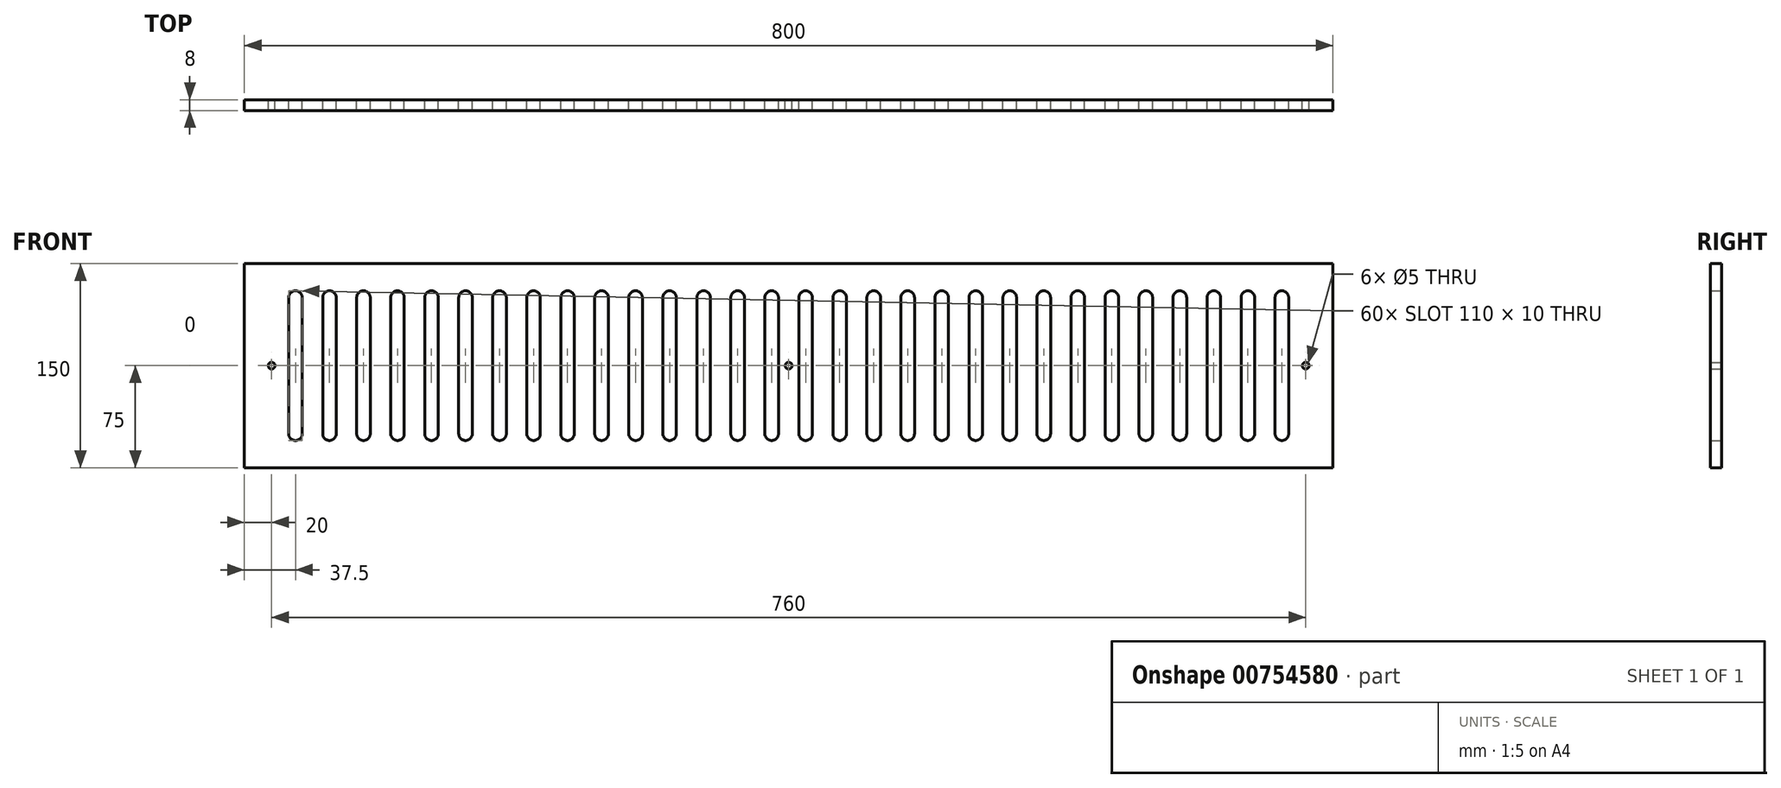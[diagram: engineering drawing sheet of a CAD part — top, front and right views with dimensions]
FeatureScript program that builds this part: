
annotation { "Feature Type Name" : "Feature", "Feature Type Description" : "" }
export const myFeature = defineFeature(function(context is Context, id is Id, definition is map)
    precondition{}
    {
        {
            var Q0;
            Q0=qCreatedBy(makeId("Front.planeOp"),FACE);
            var sketch = newSketch(context, id + "F0", { "sketchPlane" : qUnion([Q0])});
            skCircle(sketch, "E0", {"center": v(0, 0) * mm, "radius": 2.5 * mm});
            skLineSegment(sketch, "E1.bottom", {"start": v(400, 75) * mm, "end": v(-400, 75) * mm});
            skLineSegment(sketch, "E1.top", {"start": v(400, -75) * mm, "end": v(-400, -75) * mm});
            skLineSegment(sketch, "E1.left", {"start": v(400, 75) * mm, "end": v(400, -75) * mm});
            skLineSegment(sketch, "E1.right", {"start": v(-400, 75) * mm, "end": v(-400, -75) * mm});
            skLineSegment(sketch, "E2", {"start": v(-400, 0) * mm, "end": v(400, 0) * mm});
            skCircle(sketch, "E3", {"center": v(-380, 0) * mm, "radius": 2.5 * mm});
            skLineSegment(sketch, "E4.bottom", {"start": v(-362.5, 55) * mm, "end": v(-362.5, 55) * mm});
            skLineSegment(sketch, "E4.top", {"start": v(-362.5, -55) * mm, "end": v(-362.5, -55) * mm});
            skLineSegment(sketch, "E4.left", {"start": v(-357.5, 50) * mm, "end": v(-357.5, -50) * mm});
            skLineSegment(sketch, "E4.right", {"start": v(-367.5, 50) * mm, "end": v(-367.5, -50) * mm});
            skPoint(sketch, "E4.middle", {"position": v(-362.5, 0) * mm});
            skPoint(sketch, "E5.visualSharp", {"position": v(-367.5, 55) * mm});
            skArc(sketch, "E5.filletArc", {"start": v(-362.5, 55) * mm, "mid": v(-366.04, 53.54) * mm, "end": v(-367.5, 50) * mm});
            skPoint(sketch, "E6.visualSharp", {"position": v(-357.5, 55) * mm});
            skArc(sketch, "E6.filletArc", {"start": v(-357.5, 50) * mm, "mid": v(-358.96, 53.54) * mm, "end": v(-362.5, 55) * mm});
            skPoint(sketch, "E7.visualSharp", {"position": v(-357.5, -55) * mm});
            skArc(sketch, "E7.filletArc", {"start": v(-362.5, -55) * mm, "mid": v(-358.96, -53.54) * mm, "end": v(-357.5, -50) * mm});
            skPoint(sketch, "E8.visualSharp", {"position": v(-367.5, -55) * mm});
            skArc(sketch, "E8.filletArc", {"start": v(-367.5, -50) * mm, "mid": v(-366.04, -53.54) * mm, "end": v(-362.5, -55) * mm});
            skLineSegment(sketch, "E9.1.0.0", {"start": v(-332.5, 50) * mm, "end": v(-332.5, -50) * mm});
            skLineSegment(sketch, "E9.1.0.1", {"start": v(-342.5, 50) * mm, "end": v(-342.5, -50) * mm});
            skPoint(sketch, "E9.1.0.2", {"position": v(-342.5, -55) * mm});
            skPoint(sketch, "E9.1.0.3", {"position": v(-342.5, 55) * mm});
            skPoint(sketch, "E9.1.0.4", {"position": v(-332.5, 55) * mm});
            skPoint(sketch, "E9.1.0.5", {"position": v(-337.5, 0) * mm});
            skPoint(sketch, "E9.1.0.6", {"position": v(-332.5, -55) * mm});
            skArc(sketch, "E9.1.0.7", {"start": v(-332.5, 50) * mm, "mid": v(-333.96, 53.54) * mm, "end": v(-337.5, 55) * mm});
            skArc(sketch, "E9.1.0.8", {"start": v(-342.5, -50) * mm, "mid": v(-341.04, -53.54) * mm, "end": v(-337.5, -55) * mm});
            skArc(sketch, "E9.1.0.9", {"start": v(-337.5, -55) * mm, "mid": v(-333.96, -53.54) * mm, "end": v(-332.5, -50) * mm});
            skArc(sketch, "E9.1.0.10", {"start": v(-337.5, 55) * mm, "mid": v(-341.04, 53.54) * mm, "end": v(-342.5, 50) * mm});
            skLineSegment(sketch, "E9.2.0.0", {"start": v(-307.5, 50) * mm, "end": v(-307.5, -50) * mm});
            skLineSegment(sketch, "E9.2.0.1", {"start": v(-317.5, 50) * mm, "end": v(-317.5, -50) * mm});
            skPoint(sketch, "E9.2.0.2", {"position": v(-317.5, -55) * mm});
            skPoint(sketch, "E9.2.0.3", {"position": v(-317.5, 55) * mm});
            skPoint(sketch, "E9.2.0.4", {"position": v(-307.5, 55) * mm});
            skPoint(sketch, "E9.2.0.5", {"position": v(-312.5, 0) * mm});
            skPoint(sketch, "E9.2.0.6", {"position": v(-307.5, -55) * mm});
            skArc(sketch, "E9.2.0.7", {"start": v(-307.5, 50) * mm, "mid": v(-308.96, 53.54) * mm, "end": v(-312.5, 55) * mm});
            skArc(sketch, "E9.2.0.8", {"start": v(-317.5, -50) * mm, "mid": v(-316.04, -53.54) * mm, "end": v(-312.5, -55) * mm});
            skArc(sketch, "E9.2.0.9", {"start": v(-312.5, -55) * mm, "mid": v(-308.96, -53.54) * mm, "end": v(-307.5, -50) * mm});
            skArc(sketch, "E9.2.0.10", {"start": v(-312.5, 55) * mm, "mid": v(-316.04, 53.54) * mm, "end": v(-317.5, 50) * mm});
            skLineSegment(sketch, "E9.3.0.0", {"start": v(-282.5, 50) * mm, "end": v(-282.5, -50) * mm});
            skLineSegment(sketch, "E9.3.0.1", {"start": v(-292.5, 50) * mm, "end": v(-292.5, -50) * mm});
            skPoint(sketch, "E9.3.0.2", {"position": v(-292.5, -55) * mm});
            skPoint(sketch, "E9.3.0.3", {"position": v(-292.5, 55) * mm});
            skPoint(sketch, "E9.3.0.4", {"position": v(-282.5, 55) * mm});
            skPoint(sketch, "E9.3.0.5", {"position": v(-287.5, 0) * mm});
            skPoint(sketch, "E9.3.0.6", {"position": v(-282.5, -55) * mm});
            skArc(sketch, "E9.3.0.7", {"start": v(-282.5, 50) * mm, "mid": v(-283.96, 53.54) * mm, "end": v(-287.5, 55) * mm});
            skArc(sketch, "E9.3.0.8", {"start": v(-292.5, -50) * mm, "mid": v(-291.04, -53.54) * mm, "end": v(-287.5, -55) * mm});
            skArc(sketch, "E9.3.0.9", {"start": v(-287.5, -55) * mm, "mid": v(-283.96, -53.54) * mm, "end": v(-282.5, -50) * mm});
            skArc(sketch, "E9.3.0.10", {"start": v(-287.5, 55) * mm, "mid": v(-291.04, 53.54) * mm, "end": v(-292.5, 50) * mm});
            skLineSegment(sketch, "E9.4.0.0", {"start": v(-257.5, 50) * mm, "end": v(-257.5, -50) * mm});
            skLineSegment(sketch, "E9.4.0.1", {"start": v(-267.5, 50) * mm, "end": v(-267.5, -50) * mm});
            skPoint(sketch, "E9.4.0.2", {"position": v(-267.5, -55) * mm});
            skPoint(sketch, "E9.4.0.3", {"position": v(-267.5, 55) * mm});
            skPoint(sketch, "E9.4.0.4", {"position": v(-257.5, 55) * mm});
            skPoint(sketch, "E9.4.0.5", {"position": v(-262.5, 0) * mm});
            skPoint(sketch, "E9.4.0.6", {"position": v(-257.5, -55) * mm});
            skArc(sketch, "E9.4.0.7", {"start": v(-257.5, 50) * mm, "mid": v(-258.96, 53.54) * mm, "end": v(-262.5, 55) * mm});
            skArc(sketch, "E9.4.0.8", {"start": v(-267.5, -50) * mm, "mid": v(-266.04, -53.54) * mm, "end": v(-262.5, -55) * mm});
            skArc(sketch, "E9.4.0.9", {"start": v(-262.5, -55) * mm, "mid": v(-258.96, -53.54) * mm, "end": v(-257.5, -50) * mm});
            skArc(sketch, "E9.4.0.10", {"start": v(-262.5, 55) * mm, "mid": v(-266.04, 53.54) * mm, "end": v(-267.5, 50) * mm});
            skLineSegment(sketch, "E9.5.0.0", {"start": v(-232.5, 50) * mm, "end": v(-232.5, -50) * mm});
            skLineSegment(sketch, "E9.5.0.1", {"start": v(-242.5, 50) * mm, "end": v(-242.5, -50) * mm});
            skPoint(sketch, "E9.5.0.2", {"position": v(-242.5, -55) * mm});
            skPoint(sketch, "E9.5.0.3", {"position": v(-242.5, 55) * mm});
            skPoint(sketch, "E9.5.0.4", {"position": v(-232.5, 55) * mm});
            skPoint(sketch, "E9.5.0.5", {"position": v(-237.5, 0) * mm});
            skPoint(sketch, "E9.5.0.6", {"position": v(-232.5, -55) * mm});
            skArc(sketch, "E9.5.0.7", {"start": v(-232.5, 50) * mm, "mid": v(-233.96, 53.54) * mm, "end": v(-237.5, 55) * mm});
            skArc(sketch, "E9.5.0.8", {"start": v(-242.5, -50) * mm, "mid": v(-241.04, -53.54) * mm, "end": v(-237.5, -55) * mm});
            skArc(sketch, "E9.5.0.9", {"start": v(-237.5, -55) * mm, "mid": v(-233.96, -53.54) * mm, "end": v(-232.5, -50) * mm});
            skArc(sketch, "E9.5.0.10", {"start": v(-237.5, 55) * mm, "mid": v(-241.04, 53.54) * mm, "end": v(-242.5, 50) * mm});
            skLineSegment(sketch, "E9.6.0.0", {"start": v(-207.5, 50) * mm, "end": v(-207.5, -50) * mm});
            skLineSegment(sketch, "E9.6.0.1", {"start": v(-217.5, 50) * mm, "end": v(-217.5, -50) * mm});
            skPoint(sketch, "E9.6.0.2", {"position": v(-217.5, -55) * mm});
            skPoint(sketch, "E9.6.0.3", {"position": v(-217.5, 55) * mm});
            skPoint(sketch, "E9.6.0.4", {"position": v(-207.5, 55) * mm});
            skPoint(sketch, "E9.6.0.5", {"position": v(-212.5, 0) * mm});
            skPoint(sketch, "E9.6.0.6", {"position": v(-207.5, -55) * mm});
            skArc(sketch, "E9.6.0.7", {"start": v(-207.5, 50) * mm, "mid": v(-208.96, 53.54) * mm, "end": v(-212.5, 55) * mm});
            skArc(sketch, "E9.6.0.8", {"start": v(-217.5, -50) * mm, "mid": v(-216.04, -53.54) * mm, "end": v(-212.5, -55) * mm});
            skArc(sketch, "E9.6.0.9", {"start": v(-212.5, -55) * mm, "mid": v(-208.96, -53.54) * mm, "end": v(-207.5, -50) * mm});
            skArc(sketch, "E9.6.0.10", {"start": v(-212.5, 55) * mm, "mid": v(-216.04, 53.54) * mm, "end": v(-217.5, 50) * mm});
            skLineSegment(sketch, "E9.7.0.0", {"start": v(-182.5, 50) * mm, "end": v(-182.5, -50) * mm});
            skLineSegment(sketch, "E9.7.0.1", {"start": v(-192.5, 50) * mm, "end": v(-192.5, -50) * mm});
            skPoint(sketch, "E9.7.0.2", {"position": v(-192.5, -55) * mm});
            skPoint(sketch, "E9.7.0.3", {"position": v(-192.5, 55) * mm});
            skPoint(sketch, "E9.7.0.4", {"position": v(-182.5, 55) * mm});
            skPoint(sketch, "E9.7.0.5", {"position": v(-187.5, 0) * mm});
            skPoint(sketch, "E9.7.0.6", {"position": v(-182.5, -55) * mm});
            skArc(sketch, "E9.7.0.7", {"start": v(-182.5, 50) * mm, "mid": v(-183.96, 53.54) * mm, "end": v(-187.5, 55) * mm});
            skArc(sketch, "E9.7.0.8", {"start": v(-192.5, -50) * mm, "mid": v(-191.04, -53.54) * mm, "end": v(-187.5, -55) * mm});
            skArc(sketch, "E9.7.0.9", {"start": v(-187.5, -55) * mm, "mid": v(-183.96, -53.54) * mm, "end": v(-182.5, -50) * mm});
            skArc(sketch, "E9.7.0.10", {"start": v(-187.5, 55) * mm, "mid": v(-191.04, 53.54) * mm, "end": v(-192.5, 50) * mm});
            skLineSegment(sketch, "E9.8.0.0", {"start": v(-157.5, 50) * mm, "end": v(-157.5, -50) * mm});
            skLineSegment(sketch, "E9.8.0.1", {"start": v(-167.5, 50) * mm, "end": v(-167.5, -50) * mm});
            skPoint(sketch, "E9.8.0.2", {"position": v(-167.5, -55) * mm});
            skPoint(sketch, "E9.8.0.3", {"position": v(-167.5, 55) * mm});
            skPoint(sketch, "E9.8.0.4", {"position": v(-157.5, 55) * mm});
            skPoint(sketch, "E9.8.0.5", {"position": v(-162.5, 0) * mm});
            skPoint(sketch, "E9.8.0.6", {"position": v(-157.5, -55) * mm});
            skArc(sketch, "E9.8.0.7", {"start": v(-157.5, 50) * mm, "mid": v(-158.96, 53.54) * mm, "end": v(-162.5, 55) * mm});
            skArc(sketch, "E9.8.0.8", {"start": v(-167.5, -50) * mm, "mid": v(-166.04, -53.54) * mm, "end": v(-162.5, -55) * mm});
            skArc(sketch, "E9.8.0.9", {"start": v(-162.5, -55) * mm, "mid": v(-158.96, -53.54) * mm, "end": v(-157.5, -50) * mm});
            skArc(sketch, "E9.8.0.10", {"start": v(-162.5, 55) * mm, "mid": v(-166.04, 53.54) * mm, "end": v(-167.5, 50) * mm});
            skLineSegment(sketch, "E9.9.0.0", {"start": v(-132.5, 50) * mm, "end": v(-132.5, -50) * mm});
            skLineSegment(sketch, "E9.9.0.1", {"start": v(-142.5, 50) * mm, "end": v(-142.5, -50) * mm});
            skPoint(sketch, "E9.9.0.2", {"position": v(-142.5, -55) * mm});
            skPoint(sketch, "E9.9.0.3", {"position": v(-142.5, 55) * mm});
            skPoint(sketch, "E9.9.0.4", {"position": v(-132.5, 55) * mm});
            skPoint(sketch, "E9.9.0.5", {"position": v(-137.5, 0) * mm});
            skPoint(sketch, "E9.9.0.6", {"position": v(-132.5, -55) * mm});
            skArc(sketch, "E9.9.0.7", {"start": v(-132.5, 50) * mm, "mid": v(-133.96, 53.54) * mm, "end": v(-137.5, 55) * mm});
            skArc(sketch, "E9.9.0.8", {"start": v(-142.5, -50) * mm, "mid": v(-141.04, -53.54) * mm, "end": v(-137.5, -55) * mm});
            skArc(sketch, "E9.9.0.9", {"start": v(-137.5, -55) * mm, "mid": v(-133.96, -53.54) * mm, "end": v(-132.5, -50) * mm});
            skArc(sketch, "E9.9.0.10", {"start": v(-137.5, 55) * mm, "mid": v(-141.04, 53.54) * mm, "end": v(-142.5, 50) * mm});
            skLineSegment(sketch, "E9.10.0.0", {"start": v(-107.5, 50) * mm, "end": v(-107.5, -50) * mm});
            skLineSegment(sketch, "E9.10.0.1", {"start": v(-117.5, 50) * mm, "end": v(-117.5, -50) * mm});
            skPoint(sketch, "E9.10.0.2", {"position": v(-117.5, -55) * mm});
            skPoint(sketch, "E9.10.0.3", {"position": v(-117.5, 55) * mm});
            skPoint(sketch, "E9.10.0.4", {"position": v(-107.5, 55) * mm});
            skPoint(sketch, "E9.10.0.5", {"position": v(-112.5, 0) * mm});
            skPoint(sketch, "E9.10.0.6", {"position": v(-107.5, -55) * mm});
            skArc(sketch, "E9.10.0.7", {"start": v(-107.5, 50) * mm, "mid": v(-108.96, 53.54) * mm, "end": v(-112.5, 55) * mm});
            skArc(sketch, "E9.10.0.8", {"start": v(-117.5, -50) * mm, "mid": v(-116.04, -53.54) * mm, "end": v(-112.5, -55) * mm});
            skArc(sketch, "E9.10.0.9", {"start": v(-112.5, -55) * mm, "mid": v(-108.96, -53.54) * mm, "end": v(-107.5, -50) * mm});
            skArc(sketch, "E9.10.0.10", {"start": v(-112.5, 55) * mm, "mid": v(-116.04, 53.54) * mm, "end": v(-117.5, 50) * mm});
            skLineSegment(sketch, "E9.11.0.0", {"start": v(-82.5, 50) * mm, "end": v(-82.5, -50) * mm});
            skLineSegment(sketch, "E9.11.0.1", {"start": v(-92.5, 50) * mm, "end": v(-92.5, -50) * mm});
            skPoint(sketch, "E9.11.0.2", {"position": v(-92.5, -55) * mm});
            skPoint(sketch, "E9.11.0.3", {"position": v(-92.5, 55) * mm});
            skPoint(sketch, "E9.11.0.4", {"position": v(-82.5, 55) * mm});
            skPoint(sketch, "E9.11.0.5", {"position": v(-87.5, 0) * mm});
            skPoint(sketch, "E9.11.0.6", {"position": v(-82.5, -55) * mm});
            skArc(sketch, "E9.11.0.7", {"start": v(-82.5, 50) * mm, "mid": v(-83.96, 53.54) * mm, "end": v(-87.5, 55) * mm});
            skArc(sketch, "E9.11.0.8", {"start": v(-92.5, -50) * mm, "mid": v(-91.04, -53.54) * mm, "end": v(-87.5, -55) * mm});
            skArc(sketch, "E9.11.0.9", {"start": v(-87.5, -55) * mm, "mid": v(-83.96, -53.54) * mm, "end": v(-82.5, -50) * mm});
            skArc(sketch, "E9.11.0.10", {"start": v(-87.5, 55) * mm, "mid": v(-91.04, 53.54) * mm, "end": v(-92.5, 50) * mm});
            skLineSegment(sketch, "E9.12.0.0", {"start": v(-57.5, 50) * mm, "end": v(-57.5, -50) * mm});
            skLineSegment(sketch, "E9.12.0.1", {"start": v(-67.5, 50) * mm, "end": v(-67.5, -50) * mm});
            skPoint(sketch, "E9.12.0.2", {"position": v(-67.5, -55) * mm});
            skPoint(sketch, "E9.12.0.3", {"position": v(-67.5, 55) * mm});
            skPoint(sketch, "E9.12.0.4", {"position": v(-57.5, 55) * mm});
            skPoint(sketch, "E9.12.0.5", {"position": v(-62.5, 0) * mm});
            skPoint(sketch, "E9.12.0.6", {"position": v(-57.5, -55) * mm});
            skArc(sketch, "E9.12.0.7", {"start": v(-57.5, 50) * mm, "mid": v(-58.96, 53.54) * mm, "end": v(-62.5, 55) * mm});
            skArc(sketch, "E9.12.0.8", {"start": v(-67.5, -50) * mm, "mid": v(-66.04, -53.54) * mm, "end": v(-62.5, -55) * mm});
            skArc(sketch, "E9.12.0.9", {"start": v(-62.5, -55) * mm, "mid": v(-58.96, -53.54) * mm, "end": v(-57.5, -50) * mm});
            skArc(sketch, "E9.12.0.10", {"start": v(-62.5, 55) * mm, "mid": v(-66.04, 53.54) * mm, "end": v(-67.5, 50) * mm});
            skLineSegment(sketch, "E9.13.0.0", {"start": v(-32.5, 50) * mm, "end": v(-32.5, -50) * mm});
            skLineSegment(sketch, "E9.13.0.1", {"start": v(-42.5, 50) * mm, "end": v(-42.5, -50) * mm});
            skPoint(sketch, "E9.13.0.2", {"position": v(-42.5, -55) * mm});
            skPoint(sketch, "E9.13.0.3", {"position": v(-42.5, 55) * mm});
            skPoint(sketch, "E9.13.0.4", {"position": v(-32.5, 55) * mm});
            skPoint(sketch, "E9.13.0.5", {"position": v(-37.5, 0) * mm});
            skPoint(sketch, "E9.13.0.6", {"position": v(-32.5, -55) * mm});
            skArc(sketch, "E9.13.0.7", {"start": v(-32.5, 50) * mm, "mid": v(-33.96, 53.54) * mm, "end": v(-37.5, 55) * mm});
            skArc(sketch, "E9.13.0.8", {"start": v(-42.5, -50) * mm, "mid": v(-41.04, -53.54) * mm, "end": v(-37.5, -55) * mm});
            skArc(sketch, "E9.13.0.9", {"start": v(-37.5, -55) * mm, "mid": v(-33.96, -53.54) * mm, "end": v(-32.5, -50) * mm});
            skArc(sketch, "E9.13.0.10", {"start": v(-37.5, 55) * mm, "mid": v(-41.04, 53.54) * mm, "end": v(-42.5, 50) * mm});
            skLineSegment(sketch, "E9.14.0.0", {"start": v(-7.5, 50) * mm, "end": v(-7.5, -50) * mm});
            skLineSegment(sketch, "E9.14.0.1", {"start": v(-17.5, 50) * mm, "end": v(-17.5, -50) * mm});
            skPoint(sketch, "E9.14.0.2", {"position": v(-17.5, -55) * mm});
            skPoint(sketch, "E9.14.0.3", {"position": v(-17.5, 55) * mm});
            skPoint(sketch, "E9.14.0.4", {"position": v(-7.5, 55) * mm});
            skPoint(sketch, "E9.14.0.5", {"position": v(-12.5, 0) * mm});
            skPoint(sketch, "E9.14.0.6", {"position": v(-7.5, -55) * mm});
            skArc(sketch, "E9.14.0.7", {"start": v(-7.5, 50) * mm, "mid": v(-8.96, 53.54) * mm, "end": v(-12.5, 55) * mm});
            skArc(sketch, "E9.14.0.8", {"start": v(-17.5, -50) * mm, "mid": v(-16.04, -53.54) * mm, "end": v(-12.5, -55) * mm});
            skArc(sketch, "E9.14.0.9", {"start": v(-12.5, -55) * mm, "mid": v(-8.96, -53.54) * mm, "end": v(-7.5, -50) * mm});
            skArc(sketch, "E9.14.0.10", {"start": v(-12.5, 55) * mm, "mid": v(-16.04, 53.54) * mm, "end": v(-17.5, 50) * mm});
            skLineSegment(sketch, "E9.15.0.0", {"start": v(17.5, 50) * mm, "end": v(17.5, -50) * mm});
            skLineSegment(sketch, "E9.15.0.1", {"start": v(7.5, 50) * mm, "end": v(7.5, -50) * mm});
            skPoint(sketch, "E9.15.0.2", {"position": v(7.5, -55) * mm});
            skPoint(sketch, "E9.15.0.3", {"position": v(7.5, 55) * mm});
            skPoint(sketch, "E9.15.0.4", {"position": v(17.5, 55) * mm});
            skPoint(sketch, "E9.15.0.5", {"position": v(12.5, 0) * mm});
            skPoint(sketch, "E9.15.0.6", {"position": v(17.5, -55) * mm});
            skArc(sketch, "E9.15.0.7", {"start": v(17.5, 50) * mm, "mid": v(16.04, 53.54) * mm, "end": v(12.5, 55) * mm});
            skArc(sketch, "E9.15.0.8", {"start": v(7.5, -50) * mm, "mid": v(8.96, -53.54) * mm, "end": v(12.5, -55) * mm});
            skArc(sketch, "E9.15.0.9", {"start": v(12.5, -55) * mm, "mid": v(16.04, -53.54) * mm, "end": v(17.5, -50) * mm});
            skArc(sketch, "E9.15.0.10", {"start": v(12.5, 55) * mm, "mid": v(8.96, 53.54) * mm, "end": v(7.5, 50) * mm});
            skLineSegment(sketch, "E9.16.0.0", {"start": v(42.5, 50) * mm, "end": v(42.5, -50) * mm});
            skLineSegment(sketch, "E9.16.0.1", {"start": v(32.5, 50) * mm, "end": v(32.5, -50) * mm});
            skPoint(sketch, "E9.16.0.2", {"position": v(32.5, -55) * mm});
            skPoint(sketch, "E9.16.0.3", {"position": v(32.5, 55) * mm});
            skPoint(sketch, "E9.16.0.4", {"position": v(42.5, 55) * mm});
            skPoint(sketch, "E9.16.0.5", {"position": v(37.5, 0) * mm});
            skPoint(sketch, "E9.16.0.6", {"position": v(42.5, -55) * mm});
            skArc(sketch, "E9.16.0.7", {"start": v(42.5, 50) * mm, "mid": v(41.04, 53.54) * mm, "end": v(37.5, 55) * mm});
            skArc(sketch, "E9.16.0.8", {"start": v(32.5, -50) * mm, "mid": v(33.96, -53.54) * mm, "end": v(37.5, -55) * mm});
            skArc(sketch, "E9.16.0.9", {"start": v(37.5, -55) * mm, "mid": v(41.04, -53.54) * mm, "end": v(42.5, -50) * mm});
            skArc(sketch, "E9.16.0.10", {"start": v(37.5, 55) * mm, "mid": v(33.96, 53.54) * mm, "end": v(32.5, 50) * mm});
            skLineSegment(sketch, "E9.17.0.0", {"start": v(67.5, 50) * mm, "end": v(67.5, -50) * mm});
            skLineSegment(sketch, "E9.17.0.1", {"start": v(57.5, 50) * mm, "end": v(57.5, -50) * mm});
            skPoint(sketch, "E9.17.0.2", {"position": v(57.5, -55) * mm});
            skPoint(sketch, "E9.17.0.3", {"position": v(57.5, 55) * mm});
            skPoint(sketch, "E9.17.0.4", {"position": v(67.5, 55) * mm});
            skPoint(sketch, "E9.17.0.5", {"position": v(62.5, 0) * mm});
            skPoint(sketch, "E9.17.0.6", {"position": v(67.5, -55) * mm});
            skArc(sketch, "E9.17.0.7", {"start": v(67.5, 50) * mm, "mid": v(66.04, 53.54) * mm, "end": v(62.5, 55) * mm});
            skArc(sketch, "E9.17.0.8", {"start": v(57.5, -50) * mm, "mid": v(58.96, -53.54) * mm, "end": v(62.5, -55) * mm});
            skArc(sketch, "E9.17.0.9", {"start": v(62.5, -55) * mm, "mid": v(66.04, -53.54) * mm, "end": v(67.5, -50) * mm});
            skArc(sketch, "E9.17.0.10", {"start": v(62.5, 55) * mm, "mid": v(58.96, 53.54) * mm, "end": v(57.5, 50) * mm});
            skLineSegment(sketch, "E9.18.0.0", {"start": v(92.5, 50) * mm, "end": v(92.5, -50) * mm});
            skLineSegment(sketch, "E9.18.0.1", {"start": v(82.5, 50) * mm, "end": v(82.5, -50) * mm});
            skPoint(sketch, "E9.18.0.2", {"position": v(82.5, -55) * mm});
            skPoint(sketch, "E9.18.0.3", {"position": v(82.5, 55) * mm});
            skPoint(sketch, "E9.18.0.4", {"position": v(92.5, 55) * mm});
            skPoint(sketch, "E9.18.0.5", {"position": v(87.5, 0) * mm});
            skPoint(sketch, "E9.18.0.6", {"position": v(92.5, -55) * mm});
            skArc(sketch, "E9.18.0.7", {"start": v(92.5, 50) * mm, "mid": v(91.04, 53.54) * mm, "end": v(87.5, 55) * mm});
            skArc(sketch, "E9.18.0.8", {"start": v(82.5, -50) * mm, "mid": v(83.96, -53.54) * mm, "end": v(87.5, -55) * mm});
            skArc(sketch, "E9.18.0.9", {"start": v(87.5, -55) * mm, "mid": v(91.04, -53.54) * mm, "end": v(92.5, -50) * mm});
            skArc(sketch, "E9.18.0.10", {"start": v(87.5, 55) * mm, "mid": v(83.96, 53.54) * mm, "end": v(82.5, 50) * mm});
            skLineSegment(sketch, "E9.19.0.0", {"start": v(117.5, 50) * mm, "end": v(117.5, -50) * mm});
            skLineSegment(sketch, "E9.19.0.1", {"start": v(107.5, 50) * mm, "end": v(107.5, -50) * mm});
            skPoint(sketch, "E9.19.0.2", {"position": v(107.5, -55) * mm});
            skPoint(sketch, "E9.19.0.3", {"position": v(107.5, 55) * mm});
            skPoint(sketch, "E9.19.0.4", {"position": v(117.5, 55) * mm});
            skPoint(sketch, "E9.19.0.5", {"position": v(112.5, 0) * mm});
            skPoint(sketch, "E9.19.0.6", {"position": v(117.5, -55) * mm});
            skArc(sketch, "E9.19.0.7", {"start": v(117.5, 50) * mm, "mid": v(116.04, 53.54) * mm, "end": v(112.5, 55) * mm});
            skArc(sketch, "E9.19.0.8", {"start": v(107.5, -50) * mm, "mid": v(108.96, -53.54) * mm, "end": v(112.5, -55) * mm});
            skArc(sketch, "E9.19.0.9", {"start": v(112.5, -55) * mm, "mid": v(116.04, -53.54) * mm, "end": v(117.5, -50) * mm});
            skArc(sketch, "E9.19.0.10", {"start": v(112.5, 55) * mm, "mid": v(108.96, 53.54) * mm, "end": v(107.5, 50) * mm});
            skLineSegment(sketch, "E9.20.0.0", {"start": v(142.5, 50) * mm, "end": v(142.5, -50) * mm});
            skLineSegment(sketch, "E9.20.0.1", {"start": v(132.5, 50) * mm, "end": v(132.5, -50) * mm});
            skPoint(sketch, "E9.20.0.2", {"position": v(132.5, -55) * mm});
            skPoint(sketch, "E9.20.0.3", {"position": v(132.5, 55) * mm});
            skPoint(sketch, "E9.20.0.4", {"position": v(142.5, 55) * mm});
            skPoint(sketch, "E9.20.0.5", {"position": v(137.5, 0) * mm});
            skPoint(sketch, "E9.20.0.6", {"position": v(142.5, -55) * mm});
            skArc(sketch, "E9.20.0.7", {"start": v(142.5, 50) * mm, "mid": v(141.04, 53.54) * mm, "end": v(137.5, 55) * mm});
            skArc(sketch, "E9.20.0.8", {"start": v(132.5, -50) * mm, "mid": v(133.96, -53.54) * mm, "end": v(137.5, -55) * mm});
            skArc(sketch, "E9.20.0.9", {"start": v(137.5, -55) * mm, "mid": v(141.04, -53.54) * mm, "end": v(142.5, -50) * mm});
            skArc(sketch, "E9.20.0.10", {"start": v(137.5, 55) * mm, "mid": v(133.96, 53.54) * mm, "end": v(132.5, 50) * mm});
            skLineSegment(sketch, "E9.21.0.0", {"start": v(167.5, 50) * mm, "end": v(167.5, -50) * mm});
            skLineSegment(sketch, "E9.21.0.1", {"start": v(157.5, 50) * mm, "end": v(157.5, -50) * mm});
            skPoint(sketch, "E9.21.0.2", {"position": v(157.5, -55) * mm});
            skPoint(sketch, "E9.21.0.3", {"position": v(157.5, 55) * mm});
            skPoint(sketch, "E9.21.0.4", {"position": v(167.5, 55) * mm});
            skPoint(sketch, "E9.21.0.5", {"position": v(162.5, 0) * mm});
            skPoint(sketch, "E9.21.0.6", {"position": v(167.5, -55) * mm});
            skArc(sketch, "E9.21.0.7", {"start": v(167.5, 50) * mm, "mid": v(166.04, 53.54) * mm, "end": v(162.5, 55) * mm});
            skArc(sketch, "E9.21.0.8", {"start": v(157.5, -50) * mm, "mid": v(158.96, -53.54) * mm, "end": v(162.5, -55) * mm});
            skArc(sketch, "E9.21.0.9", {"start": v(162.5, -55) * mm, "mid": v(166.04, -53.54) * mm, "end": v(167.5, -50) * mm});
            skArc(sketch, "E9.21.0.10", {"start": v(162.5, 55) * mm, "mid": v(158.96, 53.54) * mm, "end": v(157.5, 50) * mm});
            skLineSegment(sketch, "E9.22.0.0", {"start": v(192.5, 50) * mm, "end": v(192.5, -50) * mm});
            skLineSegment(sketch, "E9.22.0.1", {"start": v(182.5, 50) * mm, "end": v(182.5, -50) * mm});
            skPoint(sketch, "E9.22.0.2", {"position": v(182.5, -55) * mm});
            skPoint(sketch, "E9.22.0.3", {"position": v(182.5, 55) * mm});
            skPoint(sketch, "E9.22.0.4", {"position": v(192.5, 55) * mm});
            skPoint(sketch, "E9.22.0.5", {"position": v(187.5, 0) * mm});
            skPoint(sketch, "E9.22.0.6", {"position": v(192.5, -55) * mm});
            skArc(sketch, "E9.22.0.7", {"start": v(192.5, 50) * mm, "mid": v(191.04, 53.54) * mm, "end": v(187.5, 55) * mm});
            skArc(sketch, "E9.22.0.8", {"start": v(182.5, -50) * mm, "mid": v(183.96, -53.54) * mm, "end": v(187.5, -55) * mm});
            skArc(sketch, "E9.22.0.9", {"start": v(187.5, -55) * mm, "mid": v(191.04, -53.54) * mm, "end": v(192.5, -50) * mm});
            skArc(sketch, "E9.22.0.10", {"start": v(187.5, 55) * mm, "mid": v(183.96, 53.54) * mm, "end": v(182.5, 50) * mm});
            skLineSegment(sketch, "E9.23.0.0", {"start": v(217.5, 50) * mm, "end": v(217.5, -50) * mm});
            skLineSegment(sketch, "E9.23.0.1", {"start": v(207.5, 50) * mm, "end": v(207.5, -50) * mm});
            skPoint(sketch, "E9.23.0.2", {"position": v(207.5, -55) * mm});
            skPoint(sketch, "E9.23.0.3", {"position": v(207.5, 55) * mm});
            skPoint(sketch, "E9.23.0.4", {"position": v(217.5, 55) * mm});
            skPoint(sketch, "E9.23.0.5", {"position": v(212.5, 0) * mm});
            skPoint(sketch, "E9.23.0.6", {"position": v(217.5, -55) * mm});
            skArc(sketch, "E9.23.0.7", {"start": v(217.5, 50) * mm, "mid": v(216.04, 53.54) * mm, "end": v(212.5, 55) * mm});
            skArc(sketch, "E9.23.0.8", {"start": v(207.5, -50) * mm, "mid": v(208.96, -53.54) * mm, "end": v(212.5, -55) * mm});
            skArc(sketch, "E9.23.0.9", {"start": v(212.5, -55) * mm, "mid": v(216.04, -53.54) * mm, "end": v(217.5, -50) * mm});
            skArc(sketch, "E9.23.0.10", {"start": v(212.5, 55) * mm, "mid": v(208.96, 53.54) * mm, "end": v(207.5, 50) * mm});
            skLineSegment(sketch, "E9.direction1", {"start": v(-367.5, -55) * mm, "end": v(-342.5, -55) * mm, "construction": true});
            skLineSegment(sketch, "E10.0.24.0", {"start": v(242.5, 50) * mm, "end": v(242.5, -50) * mm});
            skLineSegment(sketch, "E10.3.24.0", {"start": v(232.5, 50) * mm, "end": v(232.5, -50) * mm});
            skPoint(sketch, "E10.6.24.0", {"position": v(232.5, -55) * mm});
            skPoint(sketch, "E10.7.24.0", {"position": v(232.5, 55) * mm});
            skPoint(sketch, "E10.8.24.0", {"position": v(242.5, 55) * mm});
            skPoint(sketch, "E10.9.24.0", {"position": v(237.5, 0) * mm});
            skPoint(sketch, "E10.10.24.0", {"position": v(242.5, -55) * mm});
            skArc(sketch, "E10.11.24.0", {"start": v(242.5, 50) * mm, "mid": v(241.04, 53.54) * mm, "end": v(237.5, 55) * mm});
            skArc(sketch, "E10.15.24.0", {"start": v(232.5, -50) * mm, "mid": v(233.96, -53.54) * mm, "end": v(237.5, -55) * mm});
            skArc(sketch, "E10.19.24.0", {"start": v(237.5, -55) * mm, "mid": v(241.04, -53.54) * mm, "end": v(242.5, -50) * mm});
            skArc(sketch, "E10.23.24.0", {"start": v(237.5, 55) * mm, "mid": v(233.96, 53.54) * mm, "end": v(232.5, 50) * mm});
            skLineSegment(sketch, "E10.0.25.0", {"start": v(267.5, 50) * mm, "end": v(267.5, -50) * mm});
            skLineSegment(sketch, "E10.3.25.0", {"start": v(257.5, 50) * mm, "end": v(257.5, -50) * mm});
            skPoint(sketch, "E10.6.25.0", {"position": v(257.5, -55) * mm});
            skPoint(sketch, "E10.7.25.0", {"position": v(257.5, 55) * mm});
            skPoint(sketch, "E10.8.25.0", {"position": v(267.5, 55) * mm});
            skPoint(sketch, "E10.9.25.0", {"position": v(262.5, 0) * mm});
            skPoint(sketch, "E10.10.25.0", {"position": v(267.5, -55) * mm});
            skArc(sketch, "E10.11.25.0", {"start": v(267.5, 50) * mm, "mid": v(266.04, 53.54) * mm, "end": v(262.5, 55) * mm});
            skArc(sketch, "E10.15.25.0", {"start": v(257.5, -50) * mm, "mid": v(258.96, -53.54) * mm, "end": v(262.5, -55) * mm});
            skArc(sketch, "E10.19.25.0", {"start": v(262.5, -55) * mm, "mid": v(266.04, -53.54) * mm, "end": v(267.5, -50) * mm});
            skArc(sketch, "E10.23.25.0", {"start": v(262.5, 55) * mm, "mid": v(258.96, 53.54) * mm, "end": v(257.5, 50) * mm});
            skLineSegment(sketch, "E10.0.26.0", {"start": v(292.5, 50) * mm, "end": v(292.5, -50) * mm});
            skLineSegment(sketch, "E10.3.26.0", {"start": v(282.5, 50) * mm, "end": v(282.5, -50) * mm});
            skPoint(sketch, "E10.6.26.0", {"position": v(282.5, -55) * mm});
            skPoint(sketch, "E10.7.26.0", {"position": v(282.5, 55) * mm});
            skPoint(sketch, "E10.8.26.0", {"position": v(292.5, 55) * mm});
            skPoint(sketch, "E10.9.26.0", {"position": v(287.5, 0) * mm});
            skPoint(sketch, "E10.10.26.0", {"position": v(292.5, -55) * mm});
            skArc(sketch, "E10.11.26.0", {"start": v(292.5, 50) * mm, "mid": v(291.04, 53.54) * mm, "end": v(287.5, 55) * mm});
            skArc(sketch, "E10.15.26.0", {"start": v(282.5, -50) * mm, "mid": v(283.96, -53.54) * mm, "end": v(287.5, -55) * mm});
            skArc(sketch, "E10.19.26.0", {"start": v(287.5, -55) * mm, "mid": v(291.04, -53.54) * mm, "end": v(292.5, -50) * mm});
            skArc(sketch, "E10.23.26.0", {"start": v(287.5, 55) * mm, "mid": v(283.96, 53.54) * mm, "end": v(282.5, 50) * mm});
            skLineSegment(sketch, "E10.0.27.0", {"start": v(317.5, 50) * mm, "end": v(317.5, -50) * mm});
            skLineSegment(sketch, "E10.3.27.0", {"start": v(307.5, 50) * mm, "end": v(307.5, -50) * mm});
            skPoint(sketch, "E10.6.27.0", {"position": v(307.5, -55) * mm});
            skPoint(sketch, "E10.7.27.0", {"position": v(307.5, 55) * mm});
            skPoint(sketch, "E10.8.27.0", {"position": v(317.5, 55) * mm});
            skPoint(sketch, "E10.9.27.0", {"position": v(312.5, 0) * mm});
            skPoint(sketch, "E10.10.27.0", {"position": v(317.5, -55) * mm});
            skArc(sketch, "E10.11.27.0", {"start": v(317.5, 50) * mm, "mid": v(316.04, 53.54) * mm, "end": v(312.5, 55) * mm});
            skArc(sketch, "E10.15.27.0", {"start": v(307.5, -50) * mm, "mid": v(308.96, -53.54) * mm, "end": v(312.5, -55) * mm});
            skArc(sketch, "E10.19.27.0", {"start": v(312.5, -55) * mm, "mid": v(316.04, -53.54) * mm, "end": v(317.5, -50) * mm});
            skArc(sketch, "E10.23.27.0", {"start": v(312.5, 55) * mm, "mid": v(308.96, 53.54) * mm, "end": v(307.5, 50) * mm});
            skLineSegment(sketch, "E10.0.28.0", {"start": v(342.5, 50) * mm, "end": v(342.5, -50) * mm});
            skLineSegment(sketch, "E10.3.28.0", {"start": v(332.5, 50) * mm, "end": v(332.5, -50) * mm});
            skPoint(sketch, "E10.6.28.0", {"position": v(332.5, -55) * mm});
            skPoint(sketch, "E10.7.28.0", {"position": v(332.5, 55) * mm});
            skPoint(sketch, "E10.8.28.0", {"position": v(342.5, 55) * mm});
            skPoint(sketch, "E10.9.28.0", {"position": v(337.5, 0) * mm});
            skPoint(sketch, "E10.10.28.0", {"position": v(342.5, -55) * mm});
            skArc(sketch, "E10.11.28.0", {"start": v(342.5, 50) * mm, "mid": v(341.04, 53.54) * mm, "end": v(337.5, 55) * mm});
            skArc(sketch, "E10.15.28.0", {"start": v(332.5, -50) * mm, "mid": v(333.96, -53.54) * mm, "end": v(337.5, -55) * mm});
            skArc(sketch, "E10.19.28.0", {"start": v(337.5, -55) * mm, "mid": v(341.04, -53.54) * mm, "end": v(342.5, -50) * mm});
            skArc(sketch, "E10.23.28.0", {"start": v(337.5, 55) * mm, "mid": v(333.96, 53.54) * mm, "end": v(332.5, 50) * mm});
            skLineSegment(sketch, "E10.0.29.0", {"start": v(367.5, 50) * mm, "end": v(367.5, -50) * mm});
            skLineSegment(sketch, "E10.3.29.0", {"start": v(357.5, 50) * mm, "end": v(357.5, -50) * mm});
            skPoint(sketch, "E10.6.29.0", {"position": v(357.5, -55) * mm});
            skPoint(sketch, "E10.7.29.0", {"position": v(357.5, 55) * mm});
            skPoint(sketch, "E10.8.29.0", {"position": v(367.5, 55) * mm});
            skPoint(sketch, "E10.9.29.0", {"position": v(362.5, 0) * mm});
            skPoint(sketch, "E10.10.29.0", {"position": v(367.5, -55) * mm});
            skArc(sketch, "E10.11.29.0", {"start": v(367.5, 50) * mm, "mid": v(366.04, 53.54) * mm, "end": v(362.5, 55) * mm});
            skArc(sketch, "E10.15.29.0", {"start": v(357.5, -50) * mm, "mid": v(358.96, -53.54) * mm, "end": v(362.5, -55) * mm});
            skArc(sketch, "E10.19.29.0", {"start": v(362.5, -55) * mm, "mid": v(366.04, -53.54) * mm, "end": v(367.5, -50) * mm});
            skArc(sketch, "E10.23.29.0", {"start": v(362.5, 55) * mm, "mid": v(358.96, 53.54) * mm, "end": v(357.5, 50) * mm});
            skCircle(sketch, "E11", {"center": v(380, 0) * mm, "radius": 2.5 * mm});
            skSolve(sketch);
        }
        {
            var Q0;
            Q0 = qSketchRegion(id + "F0", true);
            extrude(context, id + "F1", {"entities" : qUnion([Q0]), "depth" : 8 * mm, "offsetDistance" : 25 * mm});
        }
    });
